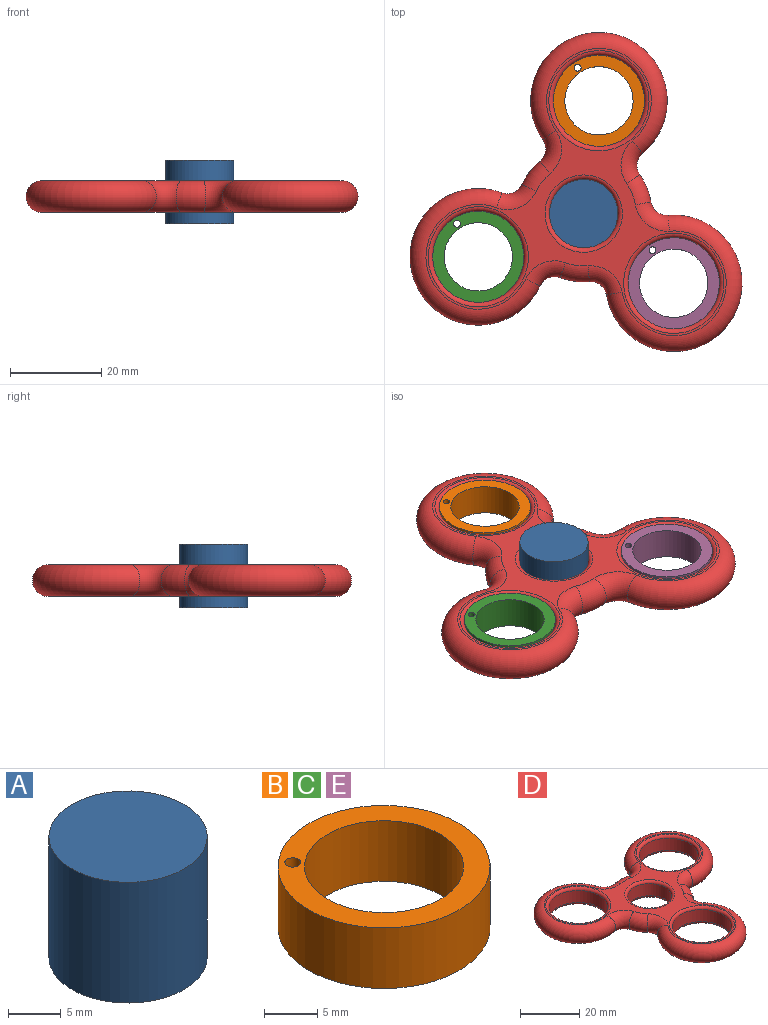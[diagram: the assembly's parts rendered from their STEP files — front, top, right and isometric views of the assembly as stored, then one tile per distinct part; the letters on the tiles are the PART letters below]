
ASSEMBLY  parts=5 mates=4
PART A: 3 faces, bbox 15x15x14 mm
  f0: cylinder r=7.5mm len=15mm, axis (0,0,-1), area 659.7mm2, adj f1,f2
  f1: plane 15x15mm, normal (0,0,1), area 176.7mm2, adj f0
  f2: plane 15x15mm, normal (0,0,-1), area 176.7mm2, adj f0
PART B: 5 faces, bbox 20x20x7 mm
  f0: cylinder r=7.5mm len=15mm, axis (0,0,-1), area 329.9mm2, adj f3,f4
  f1: cylinder r=0.75mm len=7mm, axis (0,0,-1), area 33mm2, adj f3,f4
  f2: cylinder r=10mm len=20mm, axis (0,0,-1), area 439.8mm2, adj f3,f4
  f3: plane 20x20mm, normal (0,0,1), area 135.7mm2, adj f0,f1,f2
  f4: plane 20x20mm, normal (0,0,-1), area 135.7mm2, adj f0,f1,f2
PART C: same geometry as B
PART D: 26 faces, bbox 75.8x70x7 mm
  f0: cylinder r=10mm len=20mm, axis (0,0,-1), area 314.2mm2, adj f19,f24
  f1: cylinder r=10mm len=20mm, axis (0,0,-1), area 314.2mm2, adj f20,f23
  f2: cylinder r=10mm len=20mm, axis (0,0,-1), area 314.2mm2, adj f21,f22
  f3: cylinder r=7.5mm len=15mm, axis (0,0,-1), area 235.6mm2, adj f18,f25
  f4: plane 66.3x60.5mm, normal (0,0,1), area 441.5mm2, adj f6,f7,f8,f9,f10,f11,f12,f13
  f5: plane 66.3x60.5mm, normal (0,0,-1), area 441.5mm2, adj f6,f7,f8,f9,f10,f11,f12,f13
  f6: torus R=11.5mm, axis (0,0,1), area 698.2mm2, adj f4,f5,f7,f8
  f7: torus R=7mm, axis (0,0,1), area 77.9mm2, adj f4,f5,f6,f9
  f8: torus R=7mm, axis (0,0,1), area 77.9mm2, adj f4,f5,f6,f10
  f9: torus R=11.5mm, axis (0,0,1), area 65.9mm2, adj f4,f5,f7,f11
  f10: torus R=11.5mm, axis (0,0,1), area 65.9mm2, adj f4,f5,f8,f12
  f11: torus R=7mm, axis (0,0,1), area 77.9mm2, adj f4,f5,f9,f13
  f12: torus R=7mm, axis (0,0,1), area 77.9mm2, adj f4,f5,f10,f14
  f13: torus R=11.5mm, axis (0,0,1), area 698.2mm2, adj f4,f5,f11,f16
  f14: torus R=11.5mm, axis (0,0,1), area 698.2mm2, adj f4,f5,f12,f15
  f15: torus R=7mm, axis (0,0,1), area 77.9mm2, adj f4,f5,f14,f17
  f16: torus R=7mm, axis (0,0,1), area 77.9mm2, adj f4,f5,f13,f17
  f17: torus R=11.5mm, axis (0,0,1), area 65.9mm2, adj f4,f5,f15,f16
  f18: torus R=8.5mm, axis (0,0,1), area 77.6mm2, adj f3,f5
  f19: torus R=11mm, axis (0,0,1), area 102.3mm2, adj f0,f5
  f20: torus R=11mm, axis (0,0,1), area 102.3mm2, adj f1,f5
  f21: torus R=11mm, axis (0,0,1), area 102.3mm2, adj f2,f5
  f22: torus R=11mm, axis (0,0,1), area 102.3mm2, adj f2,f4
  f23: torus R=11mm, axis (0,0,1), area 102.3mm2, adj f1,f4
  f24: torus R=11mm, axis (0,0,1), area 102.3mm2, adj f0,f4
  f25: torus R=8.5mm, axis (0,0,1), area 77.6mm2, adj f3,f4
PART E: same geometry as B
PLACE A rot(axis=(0,0,1),90deg) t=(-22.6,-2.27,-0.11)mm fixed
PLACE B rot(axis=(0,0,-1),7.7deg) t=(-19.24,22.5,2.39)mm
PLACE C rot(axis=(0,0,-1),7.7deg) t=(-45.73,-11.75,2.39)mm
PLACE D rot(axis=(1,-0.07,0),180deg) t=(-22.6,-2.27,9.39)mm
PLACE E rot(axis=(0,0,-1),7.7deg) t=(-2.82,-17.56,2.39)mm
MATE fastened E.f0 <-> D.f2  axis (0,0,1) through (-2.82,-17.56,9.39)mm
MATE fastened C.f0 <-> D.f1  axis (0,0,1) through (-45.73,-11.75,9.39)mm
MATE revolute A.f0 <-> D.f3  axis (0,0,1) through (-22.6,-2.27,13.89)mm
MATE fastened B.f0 <-> D.f0  axis (0,0,1) through (-19.24,22.5,9.39)mm
